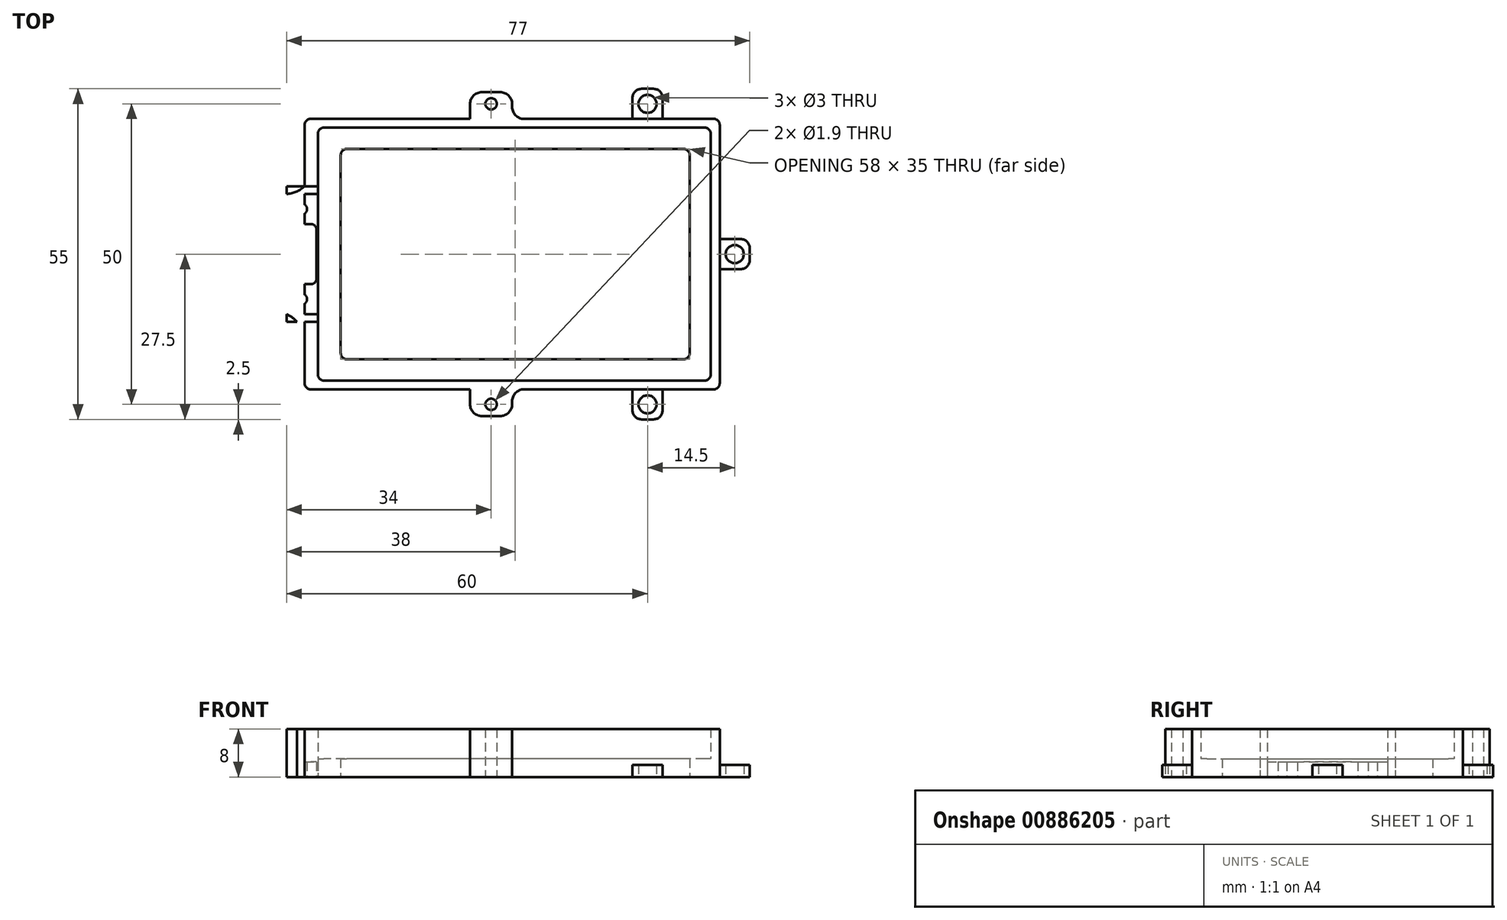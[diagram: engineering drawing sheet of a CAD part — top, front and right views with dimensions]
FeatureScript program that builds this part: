
annotation { "Feature Type Name" : "Feature", "Feature Type Description" : "" }
export const myFeature = defineFeature(function(context is Context, id is Id, definition is map)
    precondition{}
    {
        {
            var Q0;
            Q0=qCreatedBy(makeId("Top.planeOp"),FACE);
            var sketch = newSketch(context, id + "F0", { "sketchPlane" : qUnion([Q0])});
            skLineSegment(sketch, "E0.bottom", {"start": v(33.5, -22.5) * mm, "end": v(-33.5, -22.5) * mm});
            skLineSegment(sketch, "E0.top", {"start": v(33.5, 22.5) * mm, "end": v(-33.5, 22.5) * mm});
            skLineSegment(sketch, "E0.left", {"start": v(34.5, -21.5) * mm, "end": v(34.5, 21.5) * mm});
            skLineSegment(sketch, "E0.right", {"start": v(-34.5, -21.5) * mm, "end": v(-34.5, 21.5) * mm});
            skPoint(sketch, "E0.middle", {"position": v(0, 0) * mm});
            skLineSegment(sketch, "E1.bottom", {"start": v(28.5, -17.5) * mm, "end": v(-27.5, -17.5) * mm});
            skLineSegment(sketch, "E1.top", {"start": v(28.5, 17.5) * mm, "end": v(-27.5, 17.5) * mm});
            skLineSegment(sketch, "E1.left", {"start": v(29.5, -16.5) * mm, "end": v(29.5, 16.5) * mm});
            skLineSegment(sketch, "E1.right", {"start": v(-28.5, -16.5) * mm, "end": v(-28.5, 16.5) * mm});
            skPoint(sketch, "E1.middle", {"position": v(0.5, 0) * mm});
            skPoint(sketch, "E2.visualSharp", {"position": v(-28.5, 17.5) * mm});
            skArc(sketch, "E2.filletArc", {"start": v(-27.5, 17.5) * mm, "mid": v(-28.2, 17.2) * mm, "end": v(-28.5, 16.5) * mm});
            skPoint(sketch, "E3.visualSharp", {"position": v(29.5, 17.5) * mm});
            skArc(sketch, "E3.filletArc", {"start": v(29.5, 16.5) * mm, "mid": v(29.2, 17.2) * mm, "end": v(28.5, 17.5) * mm});
            skPoint(sketch, "E4.visualSharp", {"position": v(29.5, -17.5) * mm});
            skArc(sketch, "E4.filletArc", {"start": v(28.5, -17.5) * mm, "mid": v(29.2, -17.2) * mm, "end": v(29.5, -16.5) * mm});
            skPoint(sketch, "E5.visualSharp", {"position": v(-28.5, -17.5) * mm});
            skArc(sketch, "E5.filletArc", {"start": v(-28.5, -16.5) * mm, "mid": v(-28.2, -17.2) * mm, "end": v(-27.5, -17.5) * mm});
            skLineSegment(sketch, "E6.bottom", {"start": v(-37.5, 10) * mm, "end": v(-34.5, 10) * mm});
            skLineSegment(sketch, "E6.top", {"start": v(-37.5, -10) * mm, "end": v(-34.5, -10) * mm});
            skLineSegment(sketch, "E6.left", {"start": v(-37.5, 10) * mm, "end": v(-37.5, -10) * mm});
            skLineSegment(sketch, "E6.right", {"start": v(-34.5, 10) * mm, "end": v(-34.5, -10) * mm});
            skPoint(sketch, "E6.middle", {"position": v(-35, 0) * mm});
            skLineSegment(sketch, "E7.bottom", {"start": v(32, -21.05) * mm, "end": v(-31.3, -21.05) * mm});
            skLineSegment(sketch, "E7.top", {"start": v(32, 21.05) * mm, "end": v(-31.3, 21.05) * mm});
            skLineSegment(sketch, "E7.left", {"start": v(33, -20.05) * mm, "end": v(33, 20.05) * mm});
            skLineSegment(sketch, "E7.right", {"start": v(-32.3, -20.05) * mm, "end": v(-32.3, 20.05) * mm});
            skPoint(sketch, "E7.middle", {"position": v(0.35, 0) * mm});
            skPoint(sketch, "E8.visualSharp", {"position": v(-34.5, 22.5) * mm});
            skArc(sketch, "E8.filletArc", {"start": v(-33.5, 22.5) * mm, "mid": v(-34.2, 22.2) * mm, "end": v(-34.5, 21.5) * mm});
            skPoint(sketch, "E9.visualSharp", {"position": v(34.5, 22.5) * mm});
            skArc(sketch, "E9.filletArc", {"start": v(34.5, 21.5) * mm, "mid": v(34.2, 22.2) * mm, "end": v(33.5, 22.5) * mm});
            skPoint(sketch, "E10.visualSharp", {"position": v(34.5, -22.5) * mm});
            skArc(sketch, "E10.filletArc", {"start": v(33.5, -22.5) * mm, "mid": v(34.2, -22.2) * mm, "end": v(34.5, -21.5) * mm});
            skPoint(sketch, "E11.visualSharp", {"position": v(-34.5, -22.5) * mm});
            skArc(sketch, "E11.filletArc", {"start": v(-34.5, -21.5) * mm, "mid": v(-34.2, -22.2) * mm, "end": v(-33.5, -22.5) * mm});
            skPoint(sketch, "E12.visualSharp", {"position": v(33, 21.05) * mm});
            skArc(sketch, "E12.filletArc", {"start": v(33, 20.05) * mm, "mid": v(32.7, 20.76) * mm, "end": v(32, 21.05) * mm});
            skPoint(sketch, "E13.visualSharp", {"position": v(33, -21.05) * mm});
            skArc(sketch, "E13.filletArc", {"start": v(32, -21.05) * mm, "mid": v(32.7, -20.76) * mm, "end": v(33, -20.05) * mm});
            skPoint(sketch, "E14.visualSharp", {"position": v(-32.3, -21.05) * mm});
            skArc(sketch, "E14.filletArc", {"start": v(-32.3, -20.05) * mm, "mid": v(-32, -20.76) * mm, "end": v(-31.3, -21.05) * mm});
            skPoint(sketch, "E15.visualSharp", {"position": v(-32.3, 21.05) * mm});
            skArc(sketch, "E15.filletArc", {"start": v(-31.3, 21.05) * mm, "mid": v(-32, 20.76) * mm, "end": v(-32.3, 20.05) * mm});
            skCircle(sketch, "E16", {"center": v(-35, 7.5) * mm, "radius": 0.9 * mm});
            skCircle(sketch, "E17", {"center": v(-35, -7.5) * mm, "radius": 0.9 * mm});
            skLineSegment(sketch, "E18.bottom", {"start": v(-37.5, 5) * mm, "end": v(-32.5, 5) * mm});
            skLineSegment(sketch, "E18.top", {"start": v(-37.5, -5) * mm, "end": v(-32.5, -5) * mm});
            skLineSegment(sketch, "E18.left", {"start": v(-37.5, 5) * mm, "end": v(-37.5, -5) * mm});
            skLineSegment(sketch, "E19", {"start": v(-32.5, 5) * mm, "end": v(-32.5, -5) * mm});
            skLineSegment(sketch, "E20.bottom", {"start": v(-37.5, 11.25) * mm, "end": v(-32.3, 11.25) * mm});
            skLineSegment(sketch, "E20.top", {"start": v(-37.5, 10) * mm, "end": v(-32.3, 10) * mm});
            skLineSegment(sketch, "E20.left", {"start": v(-37.5, 11.25) * mm, "end": v(-37.5, 10) * mm});
            skLineSegment(sketch, "E20.right", {"start": v(-32.3, 11.25) * mm, "end": v(-32.3, 10) * mm});
            skLineSegment(sketch, "E21.bottom", {"start": v(-37.5, -10) * mm, "end": v(-32.3, -10) * mm});
            skLineSegment(sketch, "E21.top", {"start": v(-37.5, -11.25) * mm, "end": v(-32.3, -11.25) * mm});
            skLineSegment(sketch, "E21.left", {"start": v(-37.5, -10) * mm, "end": v(-37.5, -11.25) * mm});
            skLineSegment(sketch, "E21.right", {"start": v(-32.3, -10) * mm, "end": v(-32.3, -11.25) * mm});
            skSolve(sketch);
        }
        {
            var Q0;
            Q0=makeQuery(id+"F0.imprint","IMPRINT",FACE,{"disambiguationData":[TD([[makeQuery(id+"F0.imprint","IMPRINT",EDGE,{"derivedFrom":sQuery(id+"F0.wireOp",EDGE,"E0.bottom")}),-1.0]])]});
            var Q1;
            {var subQ5=sQuery(id+"F0.wireOp",EDGE,"E20.right");Q1=makeQuery(id+"F0.imprint","IMPRINT",FACE,{"disambiguationData":[TD([[makeQuery(id+"F0.imprint","IMPRINT",EDGE,{"derivedFrom":subQ5}),-1.0]])]});}
            var Q2;
            {var subQ5=sQuery(id+"F0.wireOp",EDGE,"E21.right");Q2=makeQuery(id+"F0.imprint","IMPRINT",FACE,{"disambiguationData":[TD([[makeQuery(id+"F0.imprint","IMPRINT",EDGE,{"derivedFrom":subQ5}),-1.0]])]});}
            var Q3;
            {var subQ5=sQuery(id+"F0.wireOp",EDGE,"E21.left");Q3=makeQuery(id+"F0.imprint","IMPRINT",FACE,{"disambiguationData":[TD([[makeQuery(id+"F0.imprint","IMPRINT",EDGE,{"derivedFrom":subQ5}),1.0]])]});}
            var Q4;
            {var subQ5=sQuery(id+"F0.wireOp",EDGE,"E20.left");Q4=makeQuery(id+"F0.imprint","IMPRINT",FACE,{"disambiguationData":[TD([[makeQuery(id+"F0.imprint","IMPRINT",EDGE,{"derivedFrom":subQ5}),1.0]])]});}
            extrude(context, id + "F1", {"entities" : qUnion([Q0, Q1, Q2, Q3, Q4]), "depth" : 8 * mm, "offsetDistance" : 25 * mm});
        }
        {
            var Q0;
            Q0=makeQuery(id+"F0.imprint","IMPRINT",FACE,{"disambiguationData":[TD([[makeQuery(id+"F0.imprint","IMPRINT",EDGE,{"derivedFrom":sQuery(id+"F0.wireOp",EDGE,"E1.bottom")}),1.0]])]});
            extrude(context, id + "F2", {"entities" : qUnion([Q0]), "operationType" : NewBodyOperationType.ADD, "depth" : 3 * mm, "offsetDistance" : 25 * mm});
        }
        {
            var Q0;
            {var subQ0=sQuery(id+"F0.wireOp",EDGE,"E16");var subQ1=sQuery(id+"F0.wireOp",EDGE,"E6.right");var subQ3=makeQuery(id+"F0.imprint","INTERSECT",VERTEX,{"disambiguationData":[OD(1.0)],"derivedFrom":[subQ1,subQ0]});Q0=makeQuery(id+"F0.imprint","IMPRINT",FACE,{"disambiguationData":[TD([[makeQuery(id+"F0.imprint","IMPRINT",EDGE,{"disambiguationData":[TD([[subQ3,-1.0]])],"derivedFrom":subQ1}),-1.0]])]});}
            var Q1;
            {var subQ0=sQuery(id+"F0.wireOp",EDGE,"E19");Q1=makeQuery(id+"F0.imprint","IMPRINT",FACE,{"disambiguationData":[TD([[makeQuery(id+"F0.imprint","IMPRINT",EDGE,{"derivedFrom":subQ0}),1.0]])]});}
            var Q2;
            {var subQ1=sQuery(id+"F0.wireOp",EDGE,"E6.right");var subQ6=sQuery(id+"F0.wireOp",EDGE,"E18.top");var subQ7=makeQuery(id+"F0.imprint","INTERSECT",VERTEX,{"derivedFrom":[subQ1,subQ6]});Q2=makeQuery(id+"F0.imprint","IMPRINT",FACE,{"disambiguationData":[TD([[makeQuery(id+"F0.imprint","IMPRINT",EDGE,{"disambiguationData":[TD([[subQ7,-1.0]])],"derivedFrom":subQ1}),-1.0]])]});}
            extrude(context, id + "F3", {"entities" : qUnion([Q0, Q1, Q2]), "operationType" : NewBodyOperationType.ADD, "depth" : 2.5 * mm, "offsetDistance" : 25 * mm});
        }
        {
            var Q0;
            {var subQ0=sQuery(id+"F0.wireOp",EDGE,"E0.right");var subQ1=sQuery(id+"F0.wireOp",EDGE,"E6.right");var subQ2=sQuery(id+"F0.wireOp",EDGE,"E6.top");Q0=makeQuery(id+"F3.boolean.opBoolean","SPLIT",EDGE,{"disambiguationData":[topologyDisambiguationEdgeConnected([makeQuery(id+"F1.opExtrude","SWEPT_FACE",FACE,{"disambiguationData":[OSD([subQ2])]})])],"derivedFrom":makeQuery(id+"F1.opExtrude","SWEPT_EDGE",EDGE,{"disambiguationData":[OSD([subQ0,subQ2,subQ1])]})});}
            var Q1;
            {var subQ0=sQuery(id+"F0.wireOp",EDGE,"E0.right");var subQ1=sQuery(id+"F0.wireOp",EDGE,"E6.right");var subQ2=sQuery(id+"F0.wireOp",EDGE,"E6.bottom");Q1=makeQuery(id+"F3.boolean.opBoolean","SPLIT",EDGE,{"disambiguationData":[topologyDisambiguationEdgeConnected([makeQuery(id+"F1.opExtrude","SWEPT_FACE",FACE,{"disambiguationData":[OSD([subQ2])]})])],"derivedFrom":makeQuery(id+"F1.opExtrude","SWEPT_EDGE",EDGE,{"disambiguationData":[OSD([subQ0,subQ2,subQ1])]})});}
            fillet(context, id + "F4", {"entities" : qUnion([Q0, Q1]), "radius" : 5 * mm, "tangentPropagation" : true, "allowEdgeOverflow" : false});
        }
        {
            var Q0;
            Q0=qCreatedBy(makeId("Top.planeOp"),FACE);
            var sketch = newSketch(context, id + "F5", { "sketchPlane" : qUnion([Q0])});
            skLineSegment(sketch, "E22.bottom", {"start": v(25, 22.5) * mm, "end": v(20, 22.5) * mm});
            skLineSegment(sketch, "E22.top", {"start": v(25, 27.5) * mm, "end": v(20, 27.5) * mm});
            skLineSegment(sketch, "E22.left", {"start": v(25, 22.5) * mm, "end": v(25, 27.5) * mm});
            skLineSegment(sketch, "E22.right", {"start": v(20, 22.5) * mm, "end": v(20, 27.5) * mm});
            skCircle(sketch, "E23", {"center": v(22.5, 25) * mm, "radius": 1.5 * mm});
            skLineSegment(sketch, "E24.MirrorCS", {"start": v(20, -22.5) * mm, "end": v(20, -27.5) * mm});
            skLineSegment(sketch, "E25.MirrorCS", {"start": v(25, -22.5) * mm, "end": v(20, -22.5) * mm});
            skCircle(sketch, "E26.MirrorC", {"center": v(22.5, -25) * mm, "radius": 1.5 * mm});
            skLineSegment(sketch, "E27.MirrorCS", {"start": v(25, -22.5) * mm, "end": v(25, -27.5) * mm});
            skLineSegment(sketch, "E28.MirrorCS", {"start": v(25, -27.5) * mm, "end": v(20, -27.5) * mm});
            skLineSegment(sketch, "E29.bottom", {"start": v(39.5, -2.5) * mm, "end": v(34.5, -2.5) * mm});
            skLineSegment(sketch, "E29.top", {"start": v(39.5, 2.5) * mm, "end": v(34.5, 2.5) * mm});
            skLineSegment(sketch, "E29.left", {"start": v(39.5, -2.5) * mm, "end": v(39.5, 2.5) * mm});
            skLineSegment(sketch, "E29.right", {"start": v(34.5, -2.5) * mm, "end": v(34.5, 2.5) * mm});
            skCircle(sketch, "E30", {"center": v(37, 0) * mm, "radius": 1.5 * mm});
            skSolve(sketch);
        }
        {
            var Q0;
            Q0=makeQuery(id+"F5.imprint","IMPRINT",FACE,{"disambiguationData":[TD([[makeQuery(id+"F5.imprint","IMPRINT",EDGE,{"derivedFrom":sQuery(id+"F5.wireOp",EDGE,"9qemO1Z0-uCbD-StGF-K7f1-sRLexGPPqe7a.bottom")}),-1.0]])]});
            var Q1;
            Q1=makeQuery(id+"F5.imprint","IMPRINT",FACE,{"disambiguationData":[TD([[makeQuery(id+"F5.imprint","IMPRINT",EDGE,{"derivedFrom":sQuery(id+"F5.wireOp",EDGE,"E22.bottom")}),-1.0]])]});
            var Q2;
            Q2=makeQuery(id+"F5.imprint","IMPRINT",FACE,{"disambiguationData":[TD([[makeQuery(id+"F5.imprint","IMPRINT",EDGE,{"derivedFrom":sQuery(id+"F5.wireOp",EDGE,"9bce5240-8329-4cae-a075-329807e53b990.MirrorCS")}),-1.0]])]});
            var Q3;
            Q3=makeQuery(id+"F5.imprint","IMPRINT",FACE,{"disambiguationData":[TD([[makeQuery(id+"F5.imprint","IMPRINT",EDGE,{"derivedFrom":sQuery(id+"F5.wireOp",EDGE,"E24.MirrorCS")}),1.0]])]});
            var Q4;
            Q4=makeQuery(id+"F5.imprint","IMPRINT",FACE,{"disambiguationData":[TD([[makeQuery(id+"F5.imprint","IMPRINT",EDGE,{"derivedFrom":sQuery(id+"F5.wireOp",EDGE,"E29.bottom")}),-1.0]])]});
            extrude(context, id + "F6", {"entities" : qUnion([Q0, Q1, Q2, Q3, Q4]), "operationType" : NewBodyOperationType.ADD, "depth" : 2 * mm, "offsetDistance" : 25 * mm});
        }
        {
            var Q0;
            Q0=makeQuery(id+"F6.opExtrude","SWEPT_EDGE",EDGE,{"disambiguationData":[OSD([sQuery(id+"F5.wireOp",EDGE,"E22.bottom"),sQuery(id+"F5.wireOp",EDGE,"E22.left")])]});
            var Q1;
            Q1=makeQuery(id+"F6.opExtrude","SWEPT_EDGE",EDGE,{"disambiguationData":[OSD([sQuery(id+"F5.wireOp",EDGE,"E22.top"),sQuery(id+"F5.wireOp",EDGE,"E22.left")])]});
            var Q2;
            Q2=makeQuery(id+"F6.opExtrude","SWEPT_EDGE",EDGE,{"disambiguationData":[OSD([sQuery(id+"F5.wireOp",EDGE,"E22.top"),sQuery(id+"F5.wireOp",EDGE,"E22.right")])]});
            var Q3;
            Q3=makeQuery(id+"F6.opExtrude","SWEPT_EDGE",EDGE,{"disambiguationData":[OSD([sQuery(id+"F5.wireOp",EDGE,"E22.bottom"),sQuery(id+"F5.wireOp",EDGE,"E22.right")])]});
            var Q4;
            Q4=makeQuery(id+"F6.boolean.opBoolean","INTERSECT",EDGE,{"derivedFrom":[makeQuery(id+"F1.opExtrude","SWEPT_FACE",FACE,{"disambiguationData":[OSD([sQuery(id+"F0.wireOp",EDGE,"E0.top")])]}),makeQuery(id+"F6.opExtrude","SWEPT_FACE",FACE,{"disambiguationData":[OSD([sQuery(id+"F5.wireOp",EDGE,"9qemO1Z0-uCbD-StGF-K7f1-sRLexGPPqe7a.right")])]})]});
            var Q5;
            Q5=makeQuery(id+"F6.boolean.opBoolean","INTERSECT",EDGE,{"derivedFrom":[makeQuery(id+"F1.opExtrude","SWEPT_FACE",FACE,{"disambiguationData":[OSD([sQuery(id+"F0.wireOp",EDGE,"E0.top")])]}),makeQuery(id+"F6.opExtrude","SWEPT_FACE",FACE,{"disambiguationData":[OSD([sQuery(id+"F5.wireOp",EDGE,"9qemO1Z0-uCbD-StGF-K7f1-sRLexGPPqe7a.left")])]})]});
            var Q6;
            Q6=makeQuery(id+"F6.opExtrude","SWEPT_EDGE",EDGE,{"disambiguationData":[OSD([sQuery(id+"F5.wireOp",EDGE,"9qemO1Z0-uCbD-StGF-K7f1-sRLexGPPqe7a.top"),sQuery(id+"F5.wireOp",EDGE,"9qemO1Z0-uCbD-StGF-K7f1-sRLexGPPqe7a.left")])]});
            var Q7;
            Q7=makeQuery(id+"F6.opExtrude","SWEPT_EDGE",EDGE,{"disambiguationData":[OSD([sQuery(id+"F5.wireOp",EDGE,"9qemO1Z0-uCbD-StGF-K7f1-sRLexGPPqe7a.top"),sQuery(id+"F5.wireOp",EDGE,"9qemO1Z0-uCbD-StGF-K7f1-sRLexGPPqe7a.right")])]});
            var Q8;
            Q8=makeQuery(id+"FgRZSr0Z7IsX4FJ_1.opExtrude","SWEPT_EDGE",EDGE,{"disambiguationData":[OSD([sQuery(id+"FTZmbZq8Hot6luT_1.wireOp",EDGE,"4lNVGz8E-8aNC-ndOQ-BsA1-9diXjZl0sMec.top"),sQuery(id+"FTZmbZq8Hot6luT_1.wireOp",EDGE,"4lNVGz8E-8aNC-ndOQ-BsA1-9diXjZl0sMec.right")])]});
            var Q9;
            Q9=makeQuery(id+"FgRZSr0Z7IsX4FJ_1.opExtrude","SWEPT_EDGE",EDGE,{"disambiguationData":[OSD([sQuery(id+"FTZmbZq8Hot6luT_1.wireOp",EDGE,"4lNVGz8E-8aNC-ndOQ-BsA1-9diXjZl0sMec.top"),sQuery(id+"FTZmbZq8Hot6luT_1.wireOp",EDGE,"4lNVGz8E-8aNC-ndOQ-BsA1-9diXjZl0sMec.left")])]});
            var Q10;
            Q10=makeQuery(id+"FgRZSr0Z7IsX4FJ_1.opExtrude","SWEPT_EDGE",EDGE,{"disambiguationData":[OSD([sQuery(id+"F0.wireOp",EDGE,"E0.left"),sQuery(id+"FTZmbZq8Hot6luT_1.wireOp",EDGE,"4lNVGz8E-8aNC-ndOQ-BsA1-9diXjZl0sMec.bottom"),sQuery(id+"FTZmbZq8Hot6luT_1.wireOp",EDGE,"4lNVGz8E-8aNC-ndOQ-BsA1-9diXjZl0sMec.right")])]});
            var Q11;
            Q11=makeQuery(id+"FgRZSr0Z7IsX4FJ_1.opExtrude","SWEPT_EDGE",EDGE,{"disambiguationData":[OSD([sQuery(id+"F0.wireOp",EDGE,"E0.left"),sQuery(id+"F0.wireOp",EDGE,"E9.filletArc"),sQuery(id+"FTZmbZq8Hot6luT_1.wireOp",EDGE,"4lNVGz8E-8aNC-ndOQ-BsA1-9diXjZl0sMec.bottom"),sQuery(id+"FTZmbZq8Hot6luT_1.wireOp",EDGE,"4lNVGz8E-8aNC-ndOQ-BsA1-9diXjZl0sMec.left")])]});
            var Q12;
            Q12=makeQuery(id+"F6.opExtrude","SWEPT_EDGE",EDGE,{"disambiguationData":[OSD([sQuery(id+"F5.wireOp",EDGE,"9bce5240-8329-4cae-a075-329807e53b990.MirrorCS"),sQuery(id+"F5.wireOp",EDGE,"9bce5240-8329-4cae-a075-329807e53b992.MirrorCS")])]});
            var Q13;
            Q13=makeQuery(id+"F6.boolean.opBoolean","INTERSECT",EDGE,{"derivedFrom":[makeQuery(id+"F1.opExtrude","SWEPT_FACE",FACE,{"disambiguationData":[OSD([sQuery(id+"F0.wireOp",EDGE,"E0.bottom")])]}),makeQuery(id+"F6.opExtrude","SWEPT_FACE",FACE,{"disambiguationData":[OSD([sQuery(id+"F5.wireOp",EDGE,"9bce5240-8329-4cae-a075-329807e53b990.MirrorCS")])]})]});
            var Q14;
            Q14=makeQuery(id+"F6.opExtrude","SWEPT_EDGE",EDGE,{"disambiguationData":[OSD([sQuery(id+"F5.wireOp",EDGE,"E25.MirrorCS"),sQuery(id+"F5.wireOp",EDGE,"E27.MirrorCS")])]});
            var Q15;
            Q15=makeQuery(id+"F6.opExtrude","SWEPT_EDGE",EDGE,{"disambiguationData":[OSD([sQuery(id+"F5.wireOp",EDGE,"E27.MirrorCS"),sQuery(id+"F5.wireOp",EDGE,"E28.MirrorCS")])]});
            var Q16;
            Q16=makeQuery(id+"F6.opExtrude","SWEPT_EDGE",EDGE,{"disambiguationData":[OSD([sQuery(id+"F5.wireOp",EDGE,"E24.MirrorCS"),sQuery(id+"F5.wireOp",EDGE,"E28.MirrorCS")])]});
            var Q17;
            Q17=makeQuery(id+"F6.opExtrude","SWEPT_EDGE",EDGE,{"disambiguationData":[OSD([sQuery(id+"F5.wireOp",EDGE,"E24.MirrorCS"),sQuery(id+"F5.wireOp",EDGE,"E25.MirrorCS")])]});
            var Q18;
            Q18=makeQuery(id+"F6.opExtrude","SWEPT_EDGE",EDGE,{"disambiguationData":[OSD([sQuery(id+"F5.wireOp",EDGE,"9bce5240-8329-4cae-a075-329807e53b992.MirrorCS"),sQuery(id+"F5.wireOp",EDGE,"9bce5240-8329-4cae-a075-329807e53b995.MirrorCS")])]});
            var Q19;
            Q19=makeQuery(id+"F6.boolean.opBoolean","INTERSECT",EDGE,{"derivedFrom":[makeQuery(id+"F1.opExtrude","SWEPT_FACE",FACE,{"disambiguationData":[OSD([sQuery(id+"F0.wireOp",EDGE,"E0.bottom")])]}),makeQuery(id+"F6.opExtrude","SWEPT_FACE",FACE,{"disambiguationData":[OSD([sQuery(id+"F5.wireOp",EDGE,"9bce5240-8329-4cae-a075-329807e53b995.MirrorCS")])]})]});
            var Q20;
            Q20=makeQuery(id+"F6.opExtrude","SWEPT_EDGE",EDGE,{"disambiguationData":[OSD([sQuery(id+"F5.wireOp",EDGE,"E29.bottom"),sQuery(id+"F5.wireOp",EDGE,"E29.right")])]});
            var Q21;
            Q21=makeQuery(id+"F6.opExtrude","SWEPT_EDGE",EDGE,{"disambiguationData":[OSD([sQuery(id+"F5.wireOp",EDGE,"E29.bottom"),sQuery(id+"F5.wireOp",EDGE,"E29.left")])]});
            var Q22;
            Q22=makeQuery(id+"F6.opExtrude","SWEPT_EDGE",EDGE,{"disambiguationData":[OSD([sQuery(id+"F5.wireOp",EDGE,"E29.top"),sQuery(id+"F5.wireOp",EDGE,"E29.right")])]});
            var Q23;
            Q23=makeQuery(id+"F6.opExtrude","SWEPT_EDGE",EDGE,{"disambiguationData":[OSD([sQuery(id+"F5.wireOp",EDGE,"E29.top"),sQuery(id+"F5.wireOp",EDGE,"E29.left")])]});
            fillet(context, id + "F7", {"entities" : qUnion([Q0, Q1, Q2, Q3, Q4, Q5, Q6, Q7, Q8, Q9, Q10, Q11, Q12, Q13, Q14, Q15, Q16, Q17, Q18, Q19, Q20, Q21, Q22, Q23]), "radius" : 1.5 * mm, "tangentPropagation" : true, "allowEdgeOverflow" : false});
        }
        {
            var Q0;
            Q0=makeQuery(id+"F0.imprint","IMPRINT",FACE,{"disambiguationData":[TD([[makeQuery(id+"F0.imprint","IMPRINT",EDGE,{"derivedFrom":sQuery(id+"F0.wireOp",EDGE,"E18.bottom")}),-1.0]])]});
            extrude(context, id + "F8", {"entities" : qUnion([Q0]), "operationType" : NewBodyOperationType.REMOVE, "depth" : 25 * mm, "offsetDistance" : 25 * mm});
        }
        {
            var Q0;
            Q0=makeQuery(id+"F3.opExtrude","SWEPT_EDGE",EDGE,{"disambiguationData":[OSD([sQuery(id+"F0.wireOp",EDGE,"E18.bottom"),sQuery(id+"F0.wireOp",EDGE,"E19")])]});
            var Q1;
            Q1=makeQuery(id+"F3.opExtrude","SWEPT_EDGE",EDGE,{"disambiguationData":[OSD([sQuery(id+"F0.wireOp",EDGE,"E18.top"),sQuery(id+"F0.wireOp",EDGE,"E19")])]});
            var Q2;
            {var subQ0=sQuery(id+"F0.wireOp",EDGE,"E20.left");var subQ1=sQuery(id+"F0.wireOp",EDGE,"E6.left");Q2=makeQuery(id+"F4.opFillet","BLEND_EDGE",EDGE,{"blendedFrom":[makeQuery(id+"F1.opExtrude","SWEPT_EDGE",EDGE,{"disambiguationData":[OSD([sQuery(id+"F0.wireOp",EDGE,"E0.right"),sQuery(id+"F0.wireOp",EDGE,"E20.bottom")])]}),makeQuery(id+"F3.boolean.opBoolean","MERGE",FACE,{"derivedFrom":[makeQuery(id+"F1.opExtrude","SWEPT_FACE",FACE,{"disambiguationData":[OSD([subQ0])]}),makeQuery(id+"F3.opExtrude","SWEPT_FACE",FACE,{"disambiguationData":[OSD([subQ1]),TDD([makeQuery(id+"F0.imprint","IMPRINT",EDGE,{"disambiguationData":[TD([[makeQuery(id+"F0.imprint","INTERSECT",VERTEX,{"derivedFrom":[subQ1,sQuery(id+"F0.wireOp",EDGE,"E20.top"),subQ0]}),-1.0]])],"derivedFrom":subQ1})])]})]})],"blendedInto":[makeQuery(id+"F3.boolean.opBoolean","MERGE",FACE,{"derivedFrom":[makeQuery(id+"F1.opExtrude","SWEPT_FACE",FACE,{"disambiguationData":[OSD([subQ0])]}),makeQuery(id+"F3.opExtrude","SWEPT_FACE",FACE,{"disambiguationData":[OSD([subQ1]),TDD([makeQuery(id+"F0.imprint","IMPRINT",EDGE,{"disambiguationData":[TD([[makeQuery(id+"F0.imprint","INTERSECT",VERTEX,{"derivedFrom":[subQ1,sQuery(id+"F0.wireOp",EDGE,"E20.top"),subQ0]}),-1.0]])],"derivedFrom":subQ1})])]})]})]});}
            var Q3;
            {var subQ0=sQuery(id+"F0.wireOp",EDGE,"E21.left");var subQ1=sQuery(id+"F0.wireOp",EDGE,"E6.left");Q3=makeQuery(id+"F4.opFillet","BLEND_EDGE",EDGE,{"blendedFrom":[makeQuery(id+"F1.opExtrude","SWEPT_EDGE",EDGE,{"disambiguationData":[OSD([sQuery(id+"F0.wireOp",EDGE,"E0.right"),sQuery(id+"F0.wireOp",EDGE,"E21.top")])]}),makeQuery(id+"F3.boolean.opBoolean","MERGE",FACE,{"derivedFrom":[makeQuery(id+"F1.opExtrude","SWEPT_FACE",FACE,{"disambiguationData":[OSD([subQ0])]}),makeQuery(id+"F3.opExtrude","SWEPT_FACE",FACE,{"disambiguationData":[OSD([subQ1]),TDD([makeQuery(id+"F0.imprint","IMPRINT",EDGE,{"disambiguationData":[TD([[makeQuery(id+"F0.imprint","INTERSECT",VERTEX,{"derivedFrom":[subQ1,sQuery(id+"F0.wireOp",EDGE,"E21.bottom"),subQ0]}),1.0]])],"derivedFrom":subQ1})])]})]})],"blendedInto":[makeQuery(id+"F3.boolean.opBoolean","MERGE",FACE,{"derivedFrom":[makeQuery(id+"F1.opExtrude","SWEPT_FACE",FACE,{"disambiguationData":[OSD([subQ0])]}),makeQuery(id+"F3.opExtrude","SWEPT_FACE",FACE,{"disambiguationData":[OSD([subQ1]),TDD([makeQuery(id+"F0.imprint","IMPRINT",EDGE,{"disambiguationData":[TD([[makeQuery(id+"F0.imprint","INTERSECT",VERTEX,{"derivedFrom":[subQ1,sQuery(id+"F0.wireOp",EDGE,"E21.bottom"),subQ0]}),1.0]])],"derivedFrom":subQ1})])]})]})]});}
            fillet(context, id + "F9", {"entities" : qUnion([Q0, Q1, Q2, Q3]), "radius" : 1 * mm, "tangentPropagation" : true, "allowEdgeOverflow" : false});
        }
        {
            var Q0;
            Q0=qCreatedBy(makeId("Top.planeOp"),FACE);
            var sketch = newSketch(context, id + "F10", { "sketchPlane" : qUnion([Q0])});
            skLineSegment(sketch, "E31.bottom", {"start": v(0, 22.5) * mm, "end": v(-7, 22.5) * mm});
            skLineSegment(sketch, "E31.top", {"start": v(0, 26.95) * mm, "end": v(-7, 26.95) * mm});
            skLineSegment(sketch, "E31.left", {"start": v(0, 22.5) * mm, "end": v(0, 26.95) * mm});
            skLineSegment(sketch, "E31.right", {"start": v(-7, 22.5) * mm, "end": v(-7, 26.95) * mm});
            skCircle(sketch, "E32", {"center": v(-3.5, 25) * mm, "radius": 0.95 * mm});
            skPoint(sketch, "E32.centerSnap0", {"position": v(0, 24.72) * mm});
            skPoint(sketch, "E32.centerSnap1", {"position": v(-3.5, 26.95) * mm});
            skPoint(sketch, "E33.MirrorP", {"position": v(-3.5, -26.95) * mm});
            skLineSegment(sketch, "E34.MirrorCS", {"start": v(0, -22.5) * mm, "end": v(-7, -22.5) * mm});
            skLineSegment(sketch, "E35.MirrorCS", {"start": v(-7, -22.5) * mm, "end": v(-7, -26.95) * mm});
            skPoint(sketch, "E36.MirrorP", {"position": v(0, -24.72) * mm});
            skCircle(sketch, "E37.MirrorC", {"center": v(-3.5, -25) * mm, "radius": 0.95 * mm});
            skLineSegment(sketch, "E38.MirrorCS", {"start": v(0, -22.5) * mm, "end": v(0, -26.95) * mm});
            skLineSegment(sketch, "E39.MirrorCS", {"start": v(0, -26.95) * mm, "end": v(-7, -26.95) * mm});
            skSolve(sketch);
        }
        {
            var Q0;
            Q0=makeQuery(id+"F10.imprint","IMPRINT",FACE,{"disambiguationData":[TD([[makeQuery(id+"F10.imprint","IMPRINT",EDGE,{"derivedFrom":sQuery(id+"F10.wireOp",EDGE,"E31.bottom")}),-1.0]])]});
            var Q1;
            Q1=makeQuery(id+"F10.imprint","IMPRINT",FACE,{"disambiguationData":[TD([[makeQuery(id+"F10.imprint","IMPRINT",EDGE,{"derivedFrom":sQuery(id+"F10.wireOp",EDGE,"0fb296a2-dc3d-4dd0-a1d1-8a49561a93150.MirrorCS")}),1.0]])]});
            var Q2;
            Q2=makeQuery(id+"F10.imprint","IMPRINT",FACE,{"disambiguationData":[TD([[makeQuery(id+"F10.imprint","IMPRINT",EDGE,{"derivedFrom":sQuery(id+"F10.wireOp",EDGE,"E34.MirrorCS")}),1.0]])]});
            extrude(context, id + "F11", {"entities" : qUnion([Q0, Q1, Q2]), "operationType" : NewBodyOperationType.ADD, "depth" : 8 * mm, "offsetDistance" : 25 * mm});
        }
        {
            var Q0;
            Q0=makeQuery(id+"F11.opExtrude","SWEPT_EDGE",EDGE,{"disambiguationData":[OSD([sQuery(id+"F10.wireOp",EDGE,"E35.MirrorCS"),sQuery(id+"F10.wireOp",EDGE,"E39.MirrorCS")])]});
            var Q1;
            Q1=makeQuery(id+"F11.opExtrude","SWEPT_EDGE",EDGE,{"disambiguationData":[OSD([sQuery(id+"F10.wireOp",EDGE,"E38.MirrorCS"),sQuery(id+"F10.wireOp",EDGE,"E39.MirrorCS")])]});
            var Q2;
            Q2=makeQuery(id+"F11.opExtrude","SWEPT_EDGE",EDGE,{"disambiguationData":[OSD([sQuery(id+"F10.wireOp",EDGE,"E34.MirrorCS"),sQuery(id+"F10.wireOp",EDGE,"E38.MirrorCS")])]});
            var Q3;
            Q3=makeQuery(id+"F11.opExtrude","SWEPT_EDGE",EDGE,{"disambiguationData":[OSD([sQuery(id+"F10.wireOp",EDGE,"E34.MirrorCS"),sQuery(id+"F10.wireOp",EDGE,"E35.MirrorCS")])]});
            var Q4;
            Q4=makeQuery(id+"F11.opExtrude","SWEPT_EDGE",EDGE,{"disambiguationData":[OSD([sQuery(id+"F10.wireOp",EDGE,"E31.top"),sQuery(id+"F10.wireOp",EDGE,"E31.left")])]});
            var Q5;
            Q5=makeQuery(id+"F11.opExtrude","SWEPT_EDGE",EDGE,{"disambiguationData":[OSD([sQuery(id+"F10.wireOp",EDGE,"E31.bottom"),sQuery(id+"F10.wireOp",EDGE,"E31.left")])]});
            var Q6;
            Q6=makeQuery(id+"F11.opExtrude","SWEPT_EDGE",EDGE,{"disambiguationData":[OSD([sQuery(id+"F10.wireOp",EDGE,"E31.top"),sQuery(id+"F10.wireOp",EDGE,"E31.right")])]});
            var Q7;
            Q7=makeQuery(id+"F11.opExtrude","SWEPT_EDGE",EDGE,{"disambiguationData":[OSD([sQuery(id+"F10.wireOp",EDGE,"E31.bottom"),sQuery(id+"F10.wireOp",EDGE,"E31.right")])]});
            var Q8;
            Q8=makeQuery(id+"F1.opExtrude","CAP_EDGE",EDGE,{"disambiguationData":[OSD([sQuery(id+"F0.wireOp",EDGE,"E20.top")])],"isStart":false});
            var Q9;
            Q9=makeQuery(id+"F1.opExtrude","CAP_EDGE",EDGE,{"disambiguationData":[OSD([sQuery(id+"F0.wireOp",EDGE,"E21.bottom")])],"isStart":false});
            fillet(context, id + "F12", {"entities" : qUnion([Q0, Q1, Q2, Q3, Q4, Q5, Q6, Q7, Q8, Q9]), "radius" : 2 * mm, "tangentPropagation" : true, "allowEdgeOverflow" : false});
        }
    });
